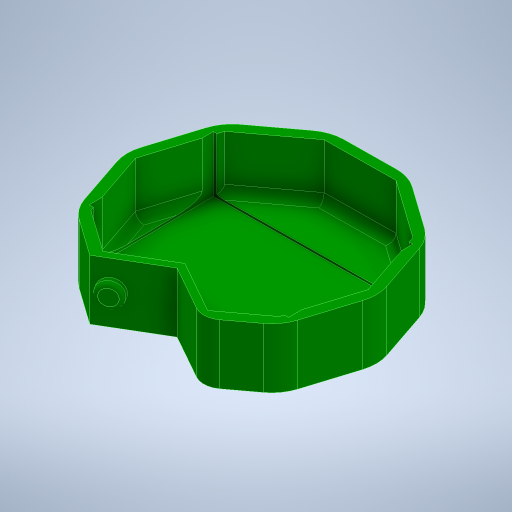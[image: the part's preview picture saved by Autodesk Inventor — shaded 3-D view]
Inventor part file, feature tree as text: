
AUTODESK INVENTOR PART (.ipt)
format: ipt  version: 2024 (Build 280153000, 153)  size: 379,904 bytes
history: native  units: in
note: dims shown in document units (in); Inventor stores cm internally (conversion verified against a paired STEP export)
features: extrude x4, fillet x4, sketch x3
ambient origin geometry x8: Origin, YZ Plane, XZ Plane, XY Plane, X Axis, Y Axis, Z Axis, Center Point
bodies: Body1 (feature_tree)
feature tree (11):
  sketch  "Sketch3"  dims[d22=2.4803in d23=0.6299in]
  extrude  "Extrusion3"  Depth=0.6299in
  extrude  "Extrusion4"  Depth=0.0669in
  extrude  "Extrusion5"  Depth=0.0591in TaperAngle=0.0deg
  fillet  "Fillet1"  Radius=0.5906in
  fillet  "Fillet2"  Radius=0.5in
  extrude  "Extrusion6"  Depth=0.1969in
  fillet  "Fillet4"  Radius=1.1811in
  fillet  "Fillet5"  Radius=0.5315in
  sketch  "Sketch4"  dims[d24=0.0984in d25=0.0669in]
  sketch  "Sketch5"  dims[d26=120.0deg d27=0.0591in d28=0.0in d29=0.5906in d30=0.0in d31=0.5in d32=1.8898in d33=1.1811in d34=0.5315in d35=0.0in d36=0.0295in d37=0.3937in d38=0.0787in d40=0.0236in d41=0.0in d42=0.0787in d43=0.0in d44=0.2362in d45=0.0394in d46=0.1969in]
